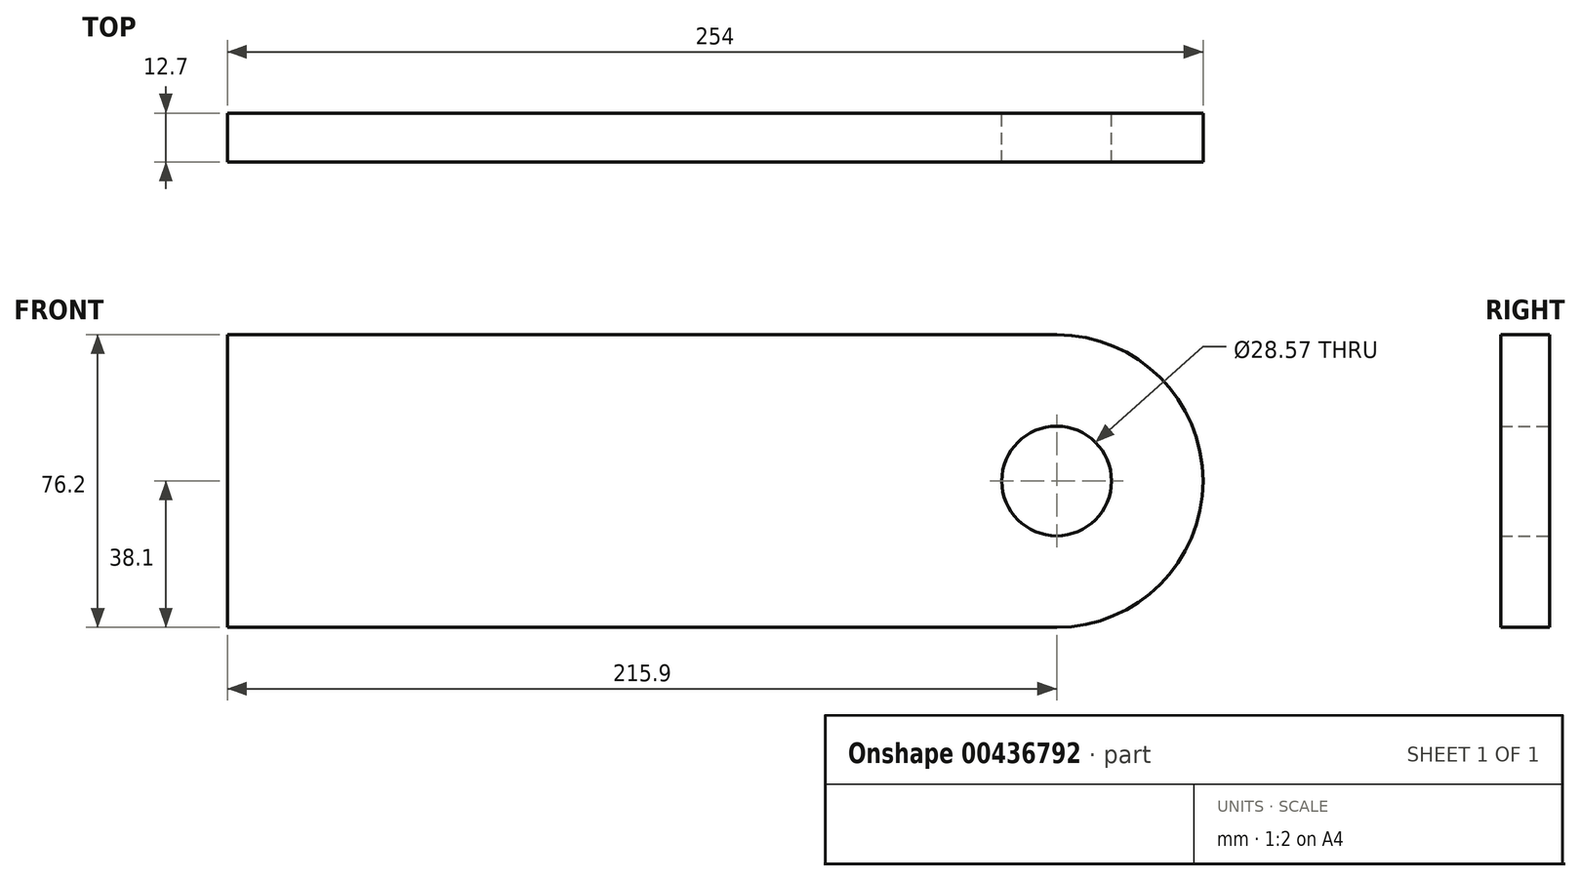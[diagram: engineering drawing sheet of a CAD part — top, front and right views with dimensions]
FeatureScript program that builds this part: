
annotation { "Feature Type Name" : "Feature", "Feature Type Description" : "" }
export const myFeature = defineFeature(function(context is Context, id is Id, definition is map)
    precondition{}
    {
        {
            var Q0;
            Q0=qCreatedBy(makeId("Front.planeOp"),FACE);
            var sketch = newSketch(context, id + "F0", { "sketchPlane" : qUnion([Q0])});
            skLineSegment(sketch, "E0.bottom", {"start": v(0, 0) * mm, "end": v(215.9, 0) * mm});
            skLineSegment(sketch, "E0.top", {"start": v(0, 76.2) * mm, "end": v(215.9, 76.2) * mm});
            skLineSegment(sketch, "E0.left", {"start": v(0, 0) * mm, "end": v(0, 76.2) * mm});
            skLineSegment(sketch, "E0.right", {"start": v(254, 38.1) * mm, "end": v(254, 38.1) * mm});
            skLineSegment(sketch, "E1", {"start": v(0, 38.1) * mm, "end": v(215.9, 38.1) * mm});
            skPoint(sketch, "E1.endSnap0", {"position": v(254, 38.1) * mm});
            skCircle(sketch, "E2", {"center": v(215.9, 38.1) * mm, "radius": 14.29 * mm});
            skPoint(sketch, "E3.visualSharp", {"position": v(254, 76.2) * mm});
            skArc(sketch, "E3.filletArc", {"start": v(254, 38.1) * mm, "mid": v(242.84, 65.04) * mm, "end": v(215.9, 76.2) * mm});
            skPoint(sketch, "E4.visualSharp", {"position": v(254, 0) * mm});
            skArc(sketch, "E4.filletArc", {"start": v(215.9, 0) * mm, "mid": v(242.84, 11.16) * mm, "end": v(254, 38.1) * mm});
            skSolve(sketch);
        }
        {
            var Q0;
            {var subQ3=sQuery(id+"F0.wireOp",EDGE,"E0.bottom");Q0=makeQuery(id+"F0.imprint","IMPRINT",FACE,{"disambiguationData":[TD([[makeQuery(id+"F0.imprint","IMPRINT",EDGE,{"derivedFrom":subQ3}),1.0]])]});}
            extrude(context, id + "F1", {"entities" : qUnion([Q0]), "depth" : 12.7 * mm});
        }
    });
